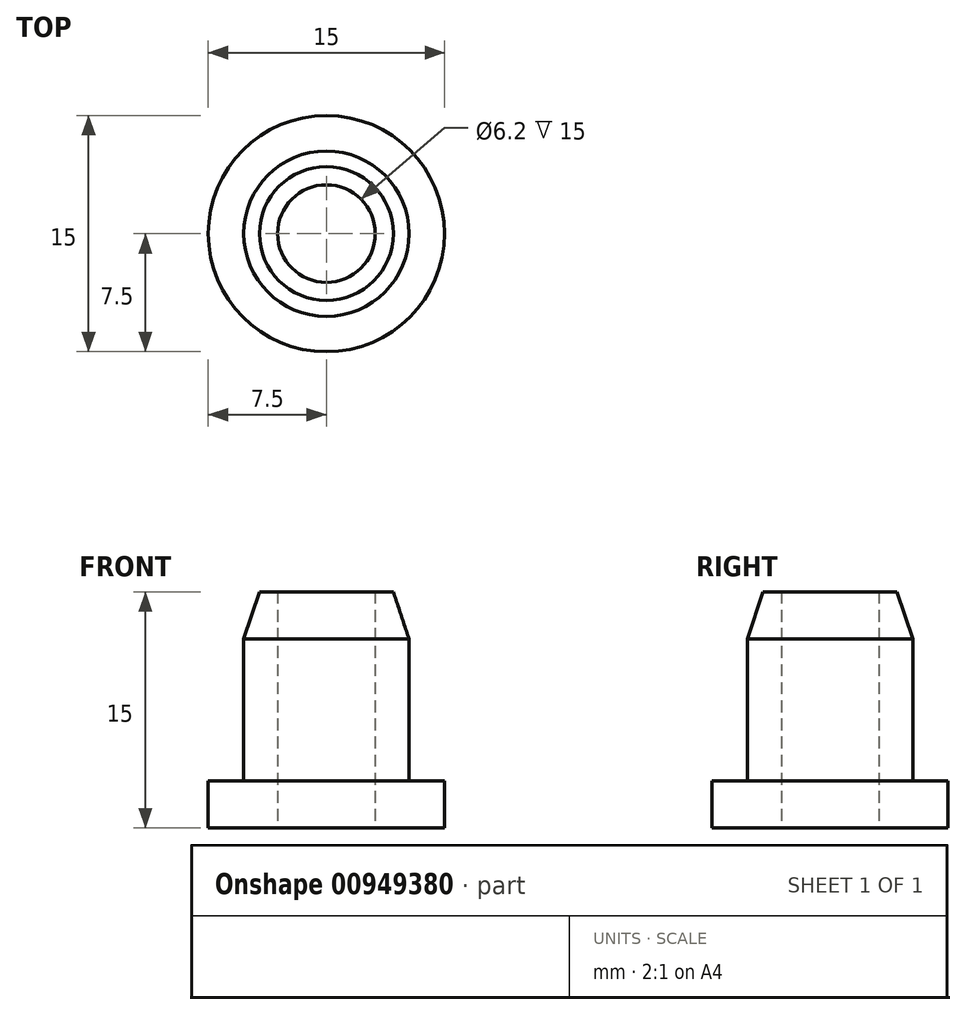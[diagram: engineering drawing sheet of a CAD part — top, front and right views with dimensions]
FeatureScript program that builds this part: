
annotation { "Feature Type Name" : "Feature", "Feature Type Description" : "" }
export const myFeature = defineFeature(function(context is Context, id is Id, definition is map)
    precondition{}
    {
        {
            var Q0;
            Q0=qCreatedBy(makeId("Top.planeOp"),FACE);
            var sketch = newSketch(context, id + "F0", { "sketchPlane" : qUnion([Q0])});
            skCircle(sketch, "E0", {"center": v(0, 0) * mm, "radius": 5.25 * mm});
            skCircle(sketch, "E1", {"center": v(0, 0) * mm, "radius": 7.5 * mm});
            skCircle(sketch, "E2", {"center": v(0, 0) * mm, "radius": 3.1 * mm});
            skSolve(sketch);
        }
        {
            var Q0;
            Q0=makeQuery(id+"F0.imprint","IMPRINT",FACE,{"disambiguationData":[TD([[makeQuery(id+"F0.imprint","IMPRINT",EDGE,{"derivedFrom":sQuery(id+"F0.wireOp",EDGE,"E0")}),1.0]])]});
            extrude(context, id + "F1", {"entities" : qUnion([Q0]), "depth" : 15 * mm, "offsetDistance" : 25 * mm});
        }
        {
            var Q0;
            Q0 = qSketchRegion(id + "F0", true);
            extrude(context, id + "F2", {"entities" : qUnion([Q0]), "operationType" : NewBodyOperationType.ADD, "depth" : 3 * mm, "offsetDistance" : 25 * mm});
        }
        {
            var Q0;
            Q0=makeQuery(id+"F1.opExtrude","CAP_EDGE",EDGE,{"disambiguationData":[OSD([sQuery(id+"F0.wireOp",EDGE,"E0")])],"isStart":false});
            chamfer(context, id + "F3", {"entities" : qUnion([Q0]), "chamferType" : ChamferType.TWO_OFFSETS, "width1" : 1 * mm, "oppositeDirection" : false, "width2" : 3 * mm, "tangentPropagation" : true});
        }
    });
